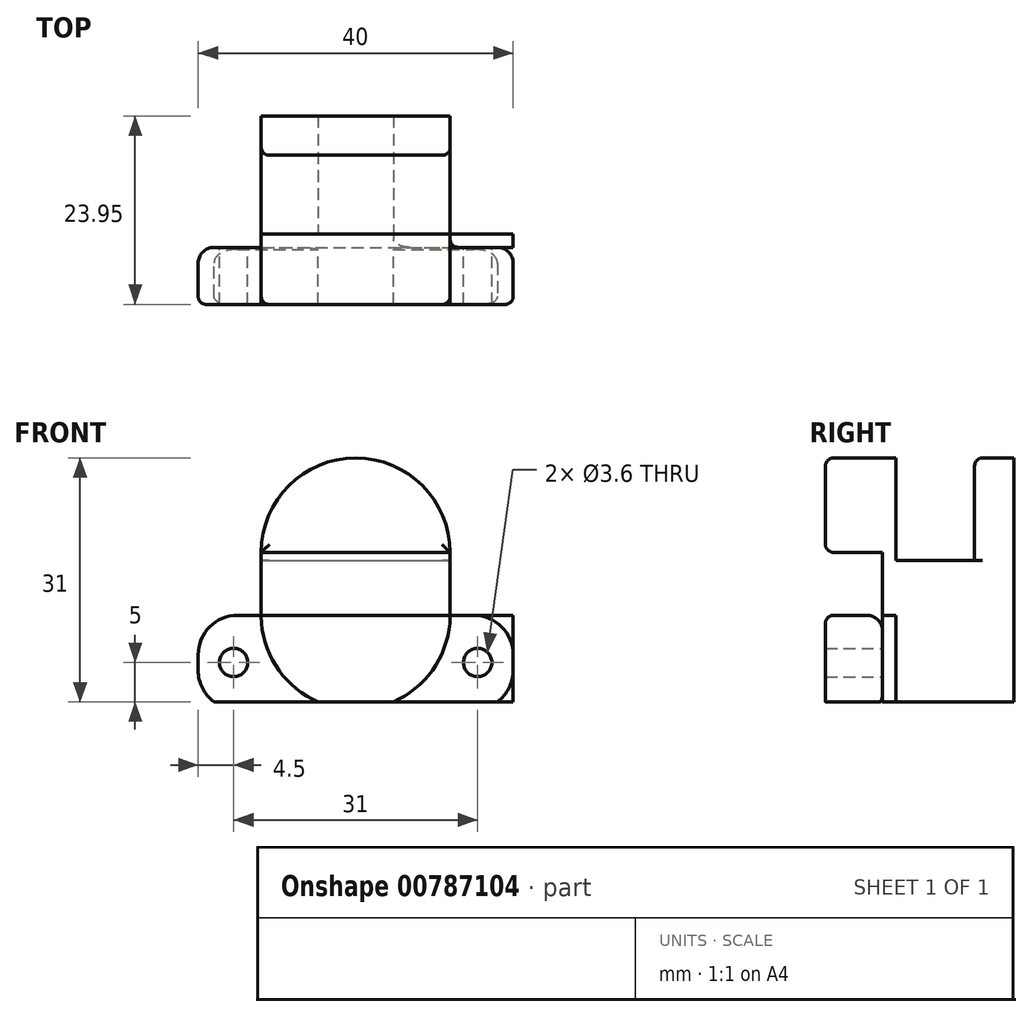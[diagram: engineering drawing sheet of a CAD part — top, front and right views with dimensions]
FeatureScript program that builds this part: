
annotation { "Feature Type Name" : "Feature", "Feature Type Description" : "" }
export const myFeature = defineFeature(function(context is Context, id is Id, definition is map)
    precondition{}
    {
        {
            var Q0;
            Q0=qCreatedBy(makeId("Front.planeOp"),FACE);
            var sketch = newSketch(context, id + "F0", { "sketchPlane" : qUnion([Q0])});
            skLineSegment(sketch, "E0.bottom", {"start": v(-20, 12) * mm, "end": v(20, 12) * mm});
            skLineSegment(sketch, "E0.top", {"start": v(-20, 0) * mm, "end": v(20, 0) * mm});
            skLineSegment(sketch, "E0.left", {"start": v(-20, 12) * mm, "end": v(-20, 0) * mm});
            skLineSegment(sketch, "E0.right", {"start": v(20, 12) * mm, "end": v(20, 0) * mm});
            skLineSegment(sketch, "E1", {"start": v(0, 20.86) * mm, "end": v(0, -29.6) * mm, "construction": true});
            skLineSegment(sketch, "E2", {"start": v(-12, 20) * mm, "end": v(12, 20) * mm});
            skArc(sketch, "E3", {"start": v(12, 20) * mm, "mid": v(0, 32) * mm, "end": v(-12, 20) * mm});
            skPoint(sketch, "E3.third.point", {"position": v(0, 32) * mm});
            skPoint(sketch, "E4.MirrorP", {"position": v(0, -26) * mm});
            skLineSegment(sketch, "E5", {"start": v(-12, 20) * mm, "end": v(-12, 12) * mm});
            skLineSegment(sketch, "E6", {"start": v(12, 20) * mm, "end": v(12, 12) * mm});
            skLineSegment(sketch, "E7", {"start": v(-31.4, 16) * mm, "end": v(45.65, 16) * mm, "construction": true});
            skLineSegment(sketch, "E8.MirrorCS", {"start": v(-12, 12) * mm, "end": v(12, 12) * mm});
            skArc(sketch, "E9.MirrorCS", {"start": v(12, 12) * mm, "mid": v(0, 0) * mm, "end": v(-12, 12) * mm});
            skSolve(sketch);
        }
        {
            var Q0;
            {var subQ0=sQuery(id+"F0.wireOp",EDGE,"E0.right");Q0=makeQuery(id+"F0.imprint","IMPRINT",FACE,{"disambiguationData":[TD([[makeQuery(id+"F0.imprint","IMPRINT",EDGE,{"derivedFrom":subQ0}),-1.0]])]});}
            var Q1;
            {var subQ0=sQuery(id+"F0.wireOp",EDGE,"E9.MirrorCS");var subQ4=makeQuery(id+"F0.imprint","INTERSECT",VERTEX,{"derivedFrom":[sQuery(id+"F0.wireOp",EDGE,"E0.top"),subQ0]});Q1=makeQuery(id+"F0.imprint","IMPRINT",FACE,{"disambiguationData":[TD([[makeQuery(id+"F0.imprint","IMPRINT",EDGE,{"disambiguationData":[TD([[subQ4,-1.0]])],"derivedFrom":subQ0}),-1.0]])]});}
            var Q2;
            {var subQ3=sQuery(id+"F0.wireOp",EDGE,"E0.left");Q2=makeQuery(id+"F0.imprint","IMPRINT",FACE,{"disambiguationData":[TD([[makeQuery(id+"F0.imprint","IMPRINT",EDGE,{"derivedFrom":subQ3}),1.0]])]});}
            var Q3;
            Q3=makeQuery(id+"F0.imprint","IMPRINT",FACE,{"disambiguationData":[TD([[makeQuery(id+"F0.imprint","IMPRINT",EDGE,{"derivedFrom":sQuery(id+"F0.wireOp",EDGE,"E2")}),1.0]])]});
            extrude(context, id + "F1", {"entities" : qUnion([Q0, Q1, Q2, Q3]), "depth" : 7.25 * mm, "offsetDistance" : 25 * mm});
        }
        {
            var Q0;
            Q0=makeQuery(id+"F0.imprint","IMPRINT",FACE,{"disambiguationData":[TD([[makeQuery(id+"F0.imprint","IMPRINT",EDGE,{"derivedFrom":sQuery(id+"F0.wireOp",EDGE,"E2")}),1.0]])]});
            var Q1;
            Q1=makeQuery(id+"F0.imprint","IMPRINT",FACE,{"disambiguationData":[TD([[makeQuery(id+"F0.imprint","IMPRINT",EDGE,{"derivedFrom":sQuery(id+"F0.wireOp",EDGE,"E2")}),-1.0]])]});
            var Q2;
            {var subQ0=sQuery(id+"F0.wireOp",EDGE,"E9.MirrorCS");var subQ4=makeQuery(id+"F0.imprint","INTERSECT",VERTEX,{"derivedFrom":[sQuery(id+"F0.wireOp",EDGE,"E0.top"),subQ0]});Q2=makeQuery(id+"F0.imprint","IMPRINT",FACE,{"disambiguationData":[TD([[makeQuery(id+"F0.imprint","IMPRINT",EDGE,{"disambiguationData":[TD([[subQ4,-1.0]])],"derivedFrom":subQ0}),-1.0]])]});}
            extrude(context, id + "F2", {"entities" : qUnion([Q0, Q1, Q2]), "oppositeDirection" : true, "depth" : 1.7 * mm, "offsetDistance" : 25 * mm});
        }
        {
            var Q0;
            Q0=makeQuery(id+"F2.opExtrude","CAP_FACE",FACE,{"disambiguationData":[OSD([sQuery(id+"F0.wireOp",EDGE,"E3"),sQuery(id+"F0.wireOp",EDGE,"E5"),sQuery(id+"F0.wireOp",EDGE,"E6"),sQuery(id+"F0.wireOp",EDGE,"E9.MirrorCS")])],"isStart":false});
            var sketch = newSketch(context, id + "F3", { "sketchPlane" : qUnion([Q0])});
            skLineSegment(sketch, "E10.0", {"start": v(12, 12) * mm, "end": v(-12, 12) * mm});
            skArc(sketch, "E10.1", {"start": v(-12, 12) * mm, "mid": v(0, 0) * mm, "end": v(12, 12) * mm});
            skSolve(sketch);
        }
        {
            var Q0;
            Q0=qSketchRegion(id+"F3",true);
            extrude(context, id + "F4", {"entities" : qUnion([Q0]), "operationType" : NewBodyOperationType.ADD, "depth" : 10 * mm, "offsetDistance" : 25 * mm});
        }
        {
            var Q0;
            Q0=makeQuery(id+"F4.opExtrude","CAP_FACE",FACE,{"disambiguationData":[OSD([sQuery(id+"F3.wireOp",EDGE,"E10.0"),sQuery(id+"F3.wireOp",EDGE,"E10.1")])],"isStart":false});
            var sketch = newSketch(context, id + "F5", { "sketchPlane" : qUnion([Q0])});
            skLineSegment(sketch, "E11.0", {"start": v(-12, 20) * mm, "end": v(-12, 12) * mm});
            skLineSegment(sketch, "E11.1", {"start": v(12, 20) * mm, "end": v(12, 12) * mm});
            skArc(sketch, "E11.2", {"start": v(-12, 20) * mm, "mid": v(0, 32) * mm, "end": v(12, 20) * mm});
            skArc(sketch, "E11.3", {"start": v(-12, 12) * mm, "mid": v(0, 0) * mm, "end": v(12, 12) * mm});
            skSolve(sketch);
        }
        {
            var Q0;
            Q0=qSketchRegion(id+"F5",true);
            extrude(context, id + "F6", {"entities" : qUnion([Q0]), "operationType" : NewBodyOperationType.ADD, "depth" : 5 * mm, "offsetDistance" : 25 * mm});
        }
        {
            var Q0;
            Q0=makeQuery(id+"F1.opExtrude","SWEPT_EDGE",EDGE,{"disambiguationData":[OSD([sQuery(id+"F0.wireOp",EDGE,"E0.bottom"),sQuery(id+"F0.wireOp",EDGE,"E0.left")])]});
            var Q1;
            Q1=makeQuery(id+"F1.opExtrude","SWEPT_EDGE",EDGE,{"disambiguationData":[OSD([sQuery(id+"F0.wireOp",EDGE,"E0.top"),sQuery(id+"F0.wireOp",EDGE,"E0.left")])]});
            var Q2;
            Q2=makeQuery(id+"F1.opExtrude","SWEPT_EDGE",EDGE,{"disambiguationData":[OSD([sQuery(id+"F0.wireOp",EDGE,"E0.bottom"),sQuery(id+"F0.wireOp",EDGE,"E0.right")])]});
            var Q3;
            Q3=makeQuery(id+"F1.opExtrude","SWEPT_EDGE",EDGE,{"disambiguationData":[OSD([sQuery(id+"F0.wireOp",EDGE,"E0.top"),sQuery(id+"F0.wireOp",EDGE,"E0.right")])]});
            fillet(context, id + "F7", {"entities" : qUnion([Q0, Q1, Q2, Q3]), "radius" : 5 * mm, "tangentPropagation" : true, "allowEdgeOverflow" : false});
        }
        {
            var Q0;
            {var subQ0=sQuery(id+"F0.wireOp",EDGE,"E0.right");Q0=makeQuery(id+"F0.imprint","IMPRINT",FACE,{"disambiguationData":[TD([[makeQuery(id+"F0.imprint","IMPRINT",EDGE,{"derivedFrom":subQ0}),-1.0]])]});}
            var sketch = newSketch(context, id + "F8", { "sketchPlane" : qUnion([Q0])});
            skCircle(sketch, "E12", {"center": v(15.5, 6) * mm, "radius": 2 * mm});
            skCircle(sketch, "E13.MirrorC", {"center": v(-15.5, 6) * mm, "radius": 2 * mm});
            skLineSegment(sketch, "E14", {"start": v(17.5, 10.05) * mm, "end": v(17.5, -2.1) * mm, "construction": true});
            skLineSegment(sketch, "E15.MirrorCS", {"start": v(-17.5, 10.05) * mm, "end": v(-17.5, -2.1) * mm, "construction": true});
            skLineSegment(sketch, "E16", {"start": v(-21.54, 6) * mm, "end": v(20.26, 6) * mm, "construction": true});
            skSolve(sketch);
        }
        {
            var Q0;
            Q0=sQuery(id+"F8.wireOp",VERTEX,"E12.center");
            var Q1;
            Q1=sQuery(id+"F8.wireOp",VERTEX,"E13.MirrorC.center");
            var Q2;
            Q2=makeQuery(id+"F1.opExtrude","SWEPT_BODY",BODY,{"disambiguationData":[OSD([sQuery(id+"F0.wireOp",EDGE,"E0.bottom"),sQuery(id+"F0.wireOp",EDGE,"E0.top"),sQuery(id+"F0.wireOp",EDGE,"E0.left"),sQuery(id+"F0.wireOp",EDGE,"E0.right")])]});
            hole(context, id + "F9", {"style" : HoleStyle.SIMPLE, "endStyle" : HoleEndStyle.THROUGH, "oppositeDirection" : true, "holeDiameter" : 3.6 * mm, "majorDiameter" : 5 * mm, "isTappedThrough" : true, "tappedDepth" : 12 * mm, "tapClearance" : 3, "locations" : qUnion([Q0, Q1]), "scope" : qUnion([Q2])});
        }
        {
            var Q0;
            Q0=makeQuery(id+"F1.opExtrude","SWEPT_BODY",BODY,{"disambiguationData":[OSD([sQuery(id+"F0.wireOp",EDGE,"E0.bottom"),sQuery(id+"F0.wireOp",EDGE,"E0.top"),sQuery(id+"F0.wireOp",EDGE,"E0.left"),sQuery(id+"F0.wireOp",EDGE,"E0.right")])]});
            var Q1;
            Q1=makeQuery(id+"F1.opExtrude","SWEPT_BODY",BODY,{"disambiguationData":[OSD([sQuery(id+"F0.wireOp",EDGE,"E2"),sQuery(id+"F0.wireOp",EDGE,"E3")])]});
            var Q2;
            Q2=makeQuery(id+"F2.opExtrude","SWEPT_BODY",BODY,{"disambiguationData":[OSD([sQuery(id+"F0.wireOp",EDGE,"E3"),sQuery(id+"F0.wireOp",EDGE,"E5"),sQuery(id+"F0.wireOp",EDGE,"E6"),sQuery(id+"F0.wireOp",EDGE,"E9.MirrorCS")])]});
            booleanBodies(context, id + "F10", {"operationType" : BooleanOperationType.UNION, "tools" : qUnion([Q0, Q1, Q2])});
        }
        {
            var Q0;
            Q0=makeQuery(id+"F4.opExtrude","SWEPT_FACE",FACE,{"disambiguationData":[OSD([sQuery(id+"F3.wireOp",EDGE,"E10.0")])]});
            extrude(context, id + "F11", {"entities" : qUnion([Q0]), "operationType" : NewBodyOperationType.ADD, "depth" : 7 * mm, "offsetDistance" : 25 * mm});
        }
        {
            var Q0;
            {var subQ0=sQuery(id+"F0.wireOp",EDGE,"E0.bottom");Q0=makeQuery(id+"F10.opBoolean","SPLIT",EDGE,{"disambiguationData":[topologyDisambiguationEdgeConnected([makeQuery(id+"F1.opExtrude","SWEPT_FACE",FACE,{"disambiguationData":[OSD([subQ0])]}),makeQuery(id+"F2.opExtrude","CAP_FACE",FACE,{"disambiguationData":[OSD([sQuery(id+"F0.wireOp",EDGE,"E3"),sQuery(id+"F0.wireOp",EDGE,"E5"),sQuery(id+"F0.wireOp",EDGE,"E6"),sQuery(id+"F0.wireOp",EDGE,"E9.MirrorCS")])],"isStart":true})])],"derivedFrom":makeQuery(id+"F1.opExtrude","CAP_EDGE",EDGE,{"disambiguationData":[OSD([subQ0])],"isStart":true})});}
            var Q1;
            Q1=makeQuery(id+"F1.opExtrude","CAP_EDGE",EDGE,{"disambiguationData":[OSD([sQuery(id+"F0.wireOp",EDGE,"E2")])],"isStart":true});
            var Q2;
            {var subQ0=sQuery(id+"F3.wireOp",EDGE,"E10.0");Q2=makeQuery(id+"F11.opExtrude","CAP_EDGE",EDGE,{"disambiguationData":[OSD([subQ0]),TDD([makeQuery(id+"F4.opExtrude","CAP_EDGE",EDGE,{"disambiguationData":[OSD([subQ0])],"isStart":true})])],"isStart":false});}
            var Q3;
            {var subQ0=sQuery(id+"F3.wireOp",EDGE,"E10.0");Q3=makeQuery(id+"F11.opExtrude","CAP_EDGE",EDGE,{"disambiguationData":[OSD([subQ0]),TDD([makeQuery(id+"F4.opExtrude","CAP_EDGE",EDGE,{"disambiguationData":[OSD([subQ0])],"isStart":false})])],"isStart":false});}
            fillet(context, id + "F12", {"entities" : qUnion([Q0, Q1, Q2, Q3]), "radius" : 2 * mm, "tangentPropagation" : true, "allowEdgeOverflow" : false});
        }
        {
            var Q0;
            Q0=makeQuery(id+"F1.opExtrude","CAP_FACE",FACE,{"disambiguationData":[OSD([sQuery(id+"F0.wireOp",EDGE,"E0.bottom"),sQuery(id+"F0.wireOp",EDGE,"E0.top"),sQuery(id+"F0.wireOp",EDGE,"E0.left"),sQuery(id+"F0.wireOp",EDGE,"E0.right")])],"isStart":false});
            var sketch = newSketch(context, id + "F13", { "sketchPlane" : qUnion([Q0])});
            skLineSegment(sketch, "E17.bottom", {"start": v(-20, 1) * mm, "end": v(20, 1) * mm});
            skLineSegment(sketch, "E17.top", {"start": v(-20, 0) * mm, "end": v(20, 0) * mm});
            skLineSegment(sketch, "E17.left", {"start": v(-20, 1) * mm, "end": v(-20, 0) * mm});
            skLineSegment(sketch, "E17.right", {"start": v(20, 1) * mm, "end": v(20, 0) * mm});
            skSolve(sketch);
        }
        {
            var Q0;
            Q0 = qSketchRegion(id + "F13", true);
            extrude(context, id + "F14", {"entities" : qUnion([Q0]), "operationType" : NewBodyOperationType.REMOVE, "endBound" : BoundingType.THROUGH_ALL, "oppositeDirection" : true, "depth" : 25 * mm, "offsetDistance" : 25 * mm});
        }
        {
            var Q0;
            Q0=makeQuery(id+"F1.opExtrude","CAP_EDGE",EDGE,{"disambiguationData":[OSD([sQuery(id+"F0.wireOp",EDGE,"E2")])],"isStart":false});
            var Q1;
            Q1=makeQuery(id+"F1.opExtrude","CAP_EDGE",EDGE,{"disambiguationData":[OSD([sQuery(id+"F0.wireOp",EDGE,"E0.bottom")])],"isStart":false});
            var Q2;
            Q2=makeQuery(id+"F1.opExtrude","CAP_EDGE",EDGE,{"disambiguationData":[OSD([sQuery(id+"F0.wireOp",EDGE,"E3")])],"isStart":false});
            var Q3;
            Q3=makeQuery(id+"F6.opExtrude","CAP_EDGE",EDGE,{"disambiguationData":[OSD([sQuery(id+"F5.wireOp",EDGE,"E11.2")])],"isStart":true});
            var Q4;
            Q4=makeQuery(id+"F14.boolean.opBoolean","COPY",EDGE,{"derivedFrom":makeQuery(id+"F14.opExtrude","CAP_EDGE",EDGE,{"disambiguationData":[OSD([sQuery(id+"F13.wireOp",EDGE,"E17.bottom")])],"isStart":true})});
            var Q5;
            {var subQ0=sQuery(id+"F0.wireOp",EDGE,"E0.left");var subQ1=sQuery(id+"F0.wireOp",EDGE,"E0.top");var subQ2=sQuery(id+"F0.wireOp",EDGE,"E8.MirrorCS");var subQ3=sQuery(id+"F0.wireOp",EDGE,"E0.right");var subQ4=sQuery(id+"F0.wireOp",EDGE,"E0.bottom");var subQ5=makeQuery(id+"F1.opExtrude","CAP_FACE",FACE,{"disambiguationData":[OSD([subQ4,subQ1,subQ0,subQ3,subQ2])],"isStart":true});var subQ6=sQuery(id+"F13.wireOp",EDGE,"E17.bottom");var subQ7=makeQuery(id+"F14.opExtrude","SWEPT_FACE",FACE,{"disambiguationData":[OSD([subQ6])]});var subQ8=dummyQuery(id+"F14.vertexPlane.planeOp",FACE);var subQ9=makeQuery(id+"F1.opExtrude","CAP_FACE",FACE,{"disambiguationData":[OSD([subQ4,subQ1,subQ0,subQ3,subQ2])],"isStart":false});var subQ11=makeQuery(id+"F13.imprint","INTERSECT",VERTEX,{"derivedFrom":[makeQuery(id+"F7.opFillet","BLEND_EDGE",EDGE,{"blendedFrom":[makeQuery(id+"F1.opExtrude","SWEPT_EDGE",EDGE,{"disambiguationData":[OSD([subQ1,subQ0])]}),subQ9],"blendedInto":[subQ9]}),subQ6]});Q5=makeQuery(id+"F14.boolean.opBoolean","COPY",EDGE,{"disambiguationData":[topologyDisambiguationEdgeConnected([subQ5,subQ7]),TD([makeQuery(id+"F7.opFillet","BLEND_FACE",FACE,{"disambiguationData":[OSD([subQ1,subQ0])]})])],"derivedFrom":makeQuery(id+"F14.opExtrude","TWEAK_EDGE",EDGE,{"derivedFrom":[makeQuery(id+"F13.imprint","IMPRINT",EDGE,{"disambiguationData":[TD([[makeQuery(id+"F13.imprint","INTERSECT",VERTEX,{"derivedFrom":[subQ6,sQuery(id+"F13.wireOp",EDGE,"E17.left")]}),-1.0]])],"derivedFrom":subQ6}),makeQuery(id+"F13.imprint","IMPRINT",EDGE,{"disambiguationData":[TD([[subQ11,-1.0]])],"derivedFrom":subQ6}),makeQuery(id+"F13.imprint","IMPRINT",EDGE,{"disambiguationData":[TD([[makeQuery(id+"F13.imprint","INTERSECT",VERTEX,{"derivedFrom":[subQ6,sQuery(id+"F13.wireOp",EDGE,"E17.right")]}),1.0]])],"derivedFrom":subQ6}),subQ8]})});}
            var Q6;
            {var subQ0=sQuery(id+"F0.wireOp",EDGE,"E9.MirrorCS");var subQ1=sQuery(id+"F0.wireOp",EDGE,"E6");var subQ2=sQuery(id+"F0.wireOp",EDGE,"E5");var subQ12=makeQuery(id+"F2.opExtrude","CAP_EDGE",EDGE,{"disambiguationData":[OSD([subQ0])],"isStart":true});Q6=qUnion([makeQuery(id+"F10.opBoolean","SPLIT",EDGE,{"disambiguationData":[TD([makeQuery(id+"F2.opExtrude","SWEPT_FACE",FACE,{"disambiguationData":[OSD([subQ2])]})])],"derivedFrom":subQ12}),makeQuery(id+"F10.opBoolean","SPLIT",EDGE,{"disambiguationData":[TD([makeQuery(id+"F2.opExtrude","SWEPT_FACE",FACE,{"disambiguationData":[OSD([subQ1])]})])],"derivedFrom":subQ12})]);}
            fillet(context, id + "F15", {"entities" : qUnion([Q0, Q1, Q2, Q3, Q4, Q5, Q6]), "radius" : 1 * mm, "tangentPropagation" : true, "allowEdgeOverflow" : false});
        }
    });
